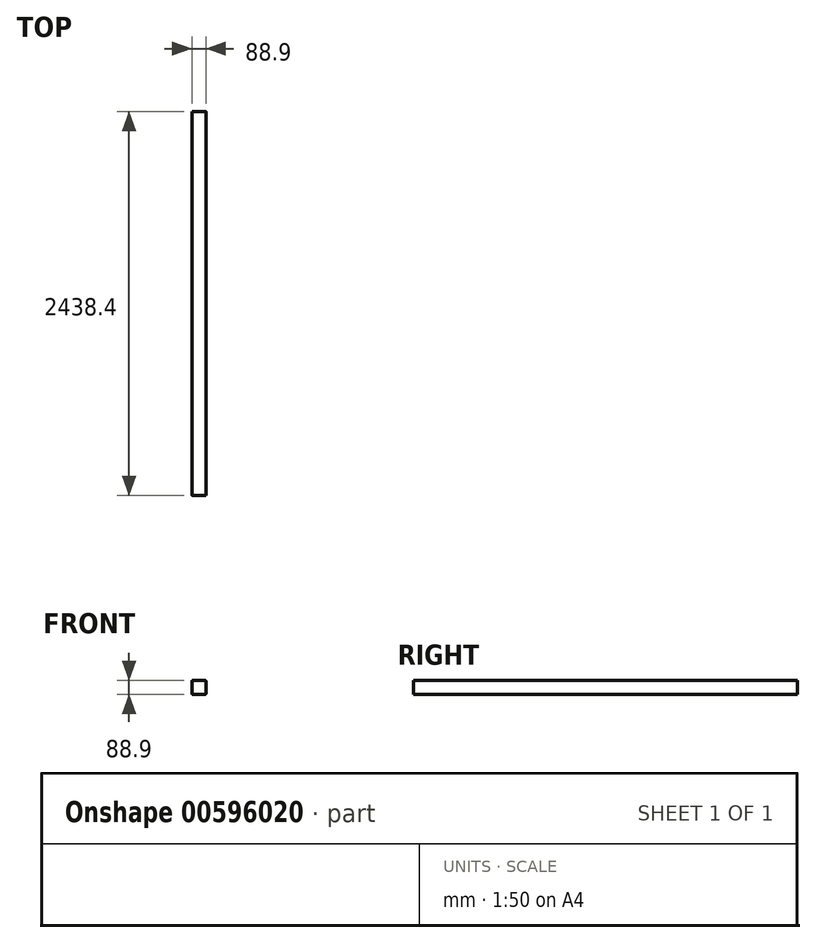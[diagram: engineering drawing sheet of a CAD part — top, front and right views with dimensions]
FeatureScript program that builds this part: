
annotation { "Feature Type Name" : "Feature", "Feature Type Description" : "" }
export const myFeature = defineFeature(function(context is Context, id is Id, definition is map)
    precondition{}
    {
        {
            var Q0;
            Q0=qCreatedBy(makeId("Front.planeOp"),FACE);
            var sketch = newSketch(context, id + "F0", { "sketchPlane" : qUnion([Q0])});
            skLineSegment(sketch, "E0.bottom", {"start": v(39.69, 44.45) * mm, "end": v(-39.69, 44.45) * mm});
            skLineSegment(sketch, "E0.top", {"start": v(39.69, -44.45) * mm, "end": v(-39.69, -44.45) * mm});
            skLineSegment(sketch, "E0.left", {"start": v(44.45, 39.69) * mm, "end": v(44.45, -39.69) * mm});
            skLineSegment(sketch, "E0.right", {"start": v(-44.45, 39.69) * mm, "end": v(-44.45, -39.69) * mm});
            skPoint(sketch, "E0.middle", {"position": v(0, 0) * mm});
            skPoint(sketch, "E1.visualSharp", {"position": v(-44.45, 44.45) * mm});
            skArc(sketch, "E1.filletArc", {"start": v(-39.69, 44.45) * mm, "mid": v(-43.06, 43.06) * mm, "end": v(-44.45, 39.69) * mm});
            skPoint(sketch, "E2.visualSharp", {"position": v(44.45, 44.45) * mm});
            skArc(sketch, "E2.filletArc", {"start": v(44.45, 39.69) * mm, "mid": v(43.06, 43.06) * mm, "end": v(39.69, 44.45) * mm});
            skPoint(sketch, "E3.visualSharp", {"position": v(44.45, -44.45) * mm});
            skArc(sketch, "E3.filletArc", {"start": v(39.69, -44.45) * mm, "mid": v(43.06, -43.06) * mm, "end": v(44.45, -39.69) * mm});
            skPoint(sketch, "E4.visualSharp", {"position": v(-44.45, -44.45) * mm});
            skArc(sketch, "E4.filletArc", {"start": v(-44.45, -39.69) * mm, "mid": v(-43.06, -43.06) * mm, "end": v(-39.69, -44.45) * mm});
            skSolve(sketch);
        }
        {
            var Q0;
            Q0=makeQuery(id+"F0.imprint","IMPRINT",FACE,{"disambiguationData":[TD([[makeQuery(id+"F0.imprint","IMPRINT",EDGE,{"derivedFrom":sQuery(id+"F0.wireOp",EDGE,"E0.bottom")}),1.0]])]});
            extrude(context, id + "F1", {"entities" : qUnion([Q0]), "depth" : 2438.4 * mm, "offsetDistance" : 25.4 * mm});
        }
    });
